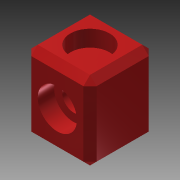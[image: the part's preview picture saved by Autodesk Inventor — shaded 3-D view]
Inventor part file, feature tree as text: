
AUTODESK INVENTOR PART (.ipt)
format: ipt  version: 2015 (Build 190159000, 159)  size: 134,144 bytes
history: native  units: mm
features: extrude x6, sketch x6, chamfer x1, projected_geometry x1
ambient origin geometry x8: Origin, YZ Plane, XZ Plane, XY Plane, X Axis, Y Axis, Z Axis, Center Point
bodies: Solide1 (feature_tree)
feature tree (14):
  extrude  "Extrusion1"  Depth=10.0mm
  extrude  "Extrusion2"  Depth=5.0mm
  extrude  "Extrusion3"  Depth=6.0mm
  extrude  "Extrusion4"  Depth=6.0mm
  extrude  "Extrusion5"  Depth=10.0mm TaperAngle=0.0deg
  extrude  "Extrusion6"  Depth=6.0mm
  chamfer  "Chanfrein1"  Distance=5.0mm
  sketch  "Esquisse1"
  sketch  "Esquisse2"
  sketch  "Esquisse3"
  sketch  "Esquisse4"
  sketch  "Esquisse5"
  projected_geometry  "Boucle projetée1"
  sketch  "Esquisse6"
